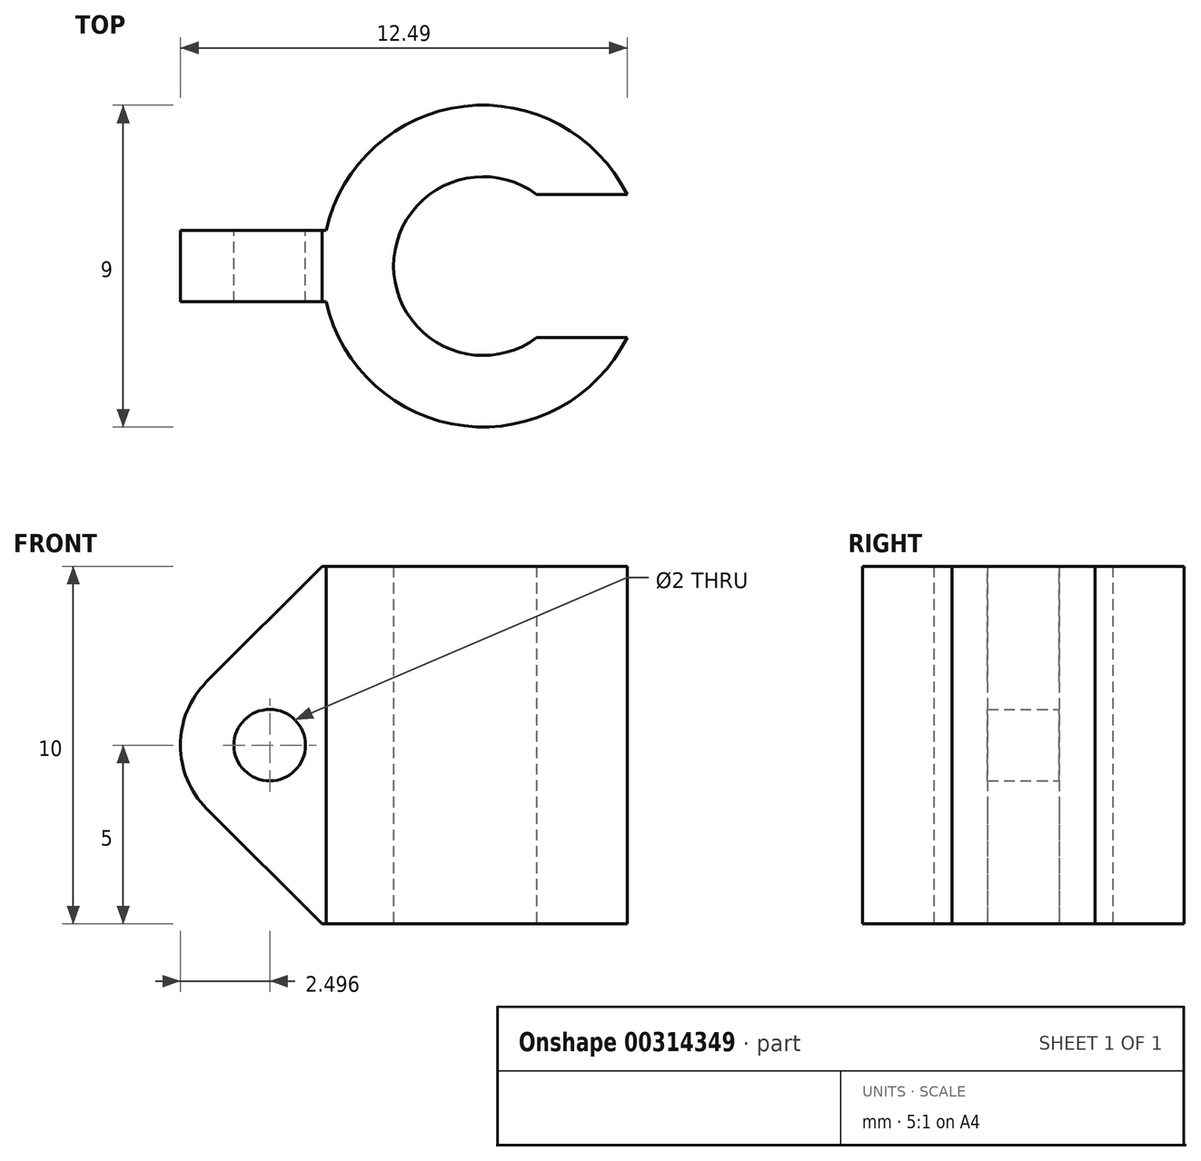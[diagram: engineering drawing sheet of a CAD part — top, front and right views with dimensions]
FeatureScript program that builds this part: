
annotation { "Feature Type Name" : "Feature", "Feature Type Description" : "" }
export const myFeature = defineFeature(function(context is Context, id is Id, definition is map)
    precondition{}
    {
        {
            var Q0;
            Q0=qCreatedBy(makeId("Top.planeOp"),FACE);
            var sketch = newSketch(context, id + "F0", { "sketchPlane" : qUnion([Q0])});
            skArc(sketch, "E0", {"start": v(4.03, 2) * mm, "mid": v(-4.5, 0) * mm, "end": v(4.03, -2) * mm});
            skArc(sketch, "E1", {"start": v(1.5, 2) * mm, "mid": v(-2.5, 0) * mm, "end": v(1.5, -2) * mm});
            skLineSegment(sketch, "E2", {"start": v(-7.9, 0) * mm, "end": v(10.8, 0) * mm, "construction": true});
            skLineSegment(sketch, "E3", {"start": v(4.03, -2) * mm, "end": v(1.5, -2) * mm});
            skLineSegment(sketch, "E4.trimOffspring", {"start": v(1.5, 2) * mm, "end": v(4.03, 2) * mm});
            skSolve(sketch);
        }
        {
            var Q0;
            Q0 = qSketchRegion(id + "F0", true);
            extrude(context, id + "F1", {"entities" : qUnion([Q0]), "depth" : 10 * mm, "offsetDistance" : 25 * mm});
        }
        {
            var Q0;
            Q0=qCreatedBy(makeId("Front.planeOp"),FACE);
            var sketch = newSketch(context, id + "F2", { "sketchPlane" : qUnion([Q0])});
            skCircle(sketch, "E5", {"center": v(-5.96, 5) * mm, "radius": 1 * mm});
            skLineSegment(sketch, "E6", {"start": v(-5.96, 5) * mm, "end": v(0, 5) * mm, "construction": true});
            skLineSegment(sketch, "E7", {"start": v(0, 0) * mm, "end": v(0, 5) * mm, "construction": true});
            skArc(sketch, "E8.0", {"start": v(-7.73, 6.77) * mm, "mid": v(-8.46, 5) * mm, "end": v(-7.73, 3.23) * mm});
            skLineSegment(sketch, "E9", {"start": v(-7.73, 6.77) * mm, "end": v(-4.5, 10) * mm});
            skLineSegment(sketch, "E10", {"start": v(-7.73, 3.23) * mm, "end": v(-4.5, 0) * mm});
            skLineSegment(sketch, "E11", {"start": v(-4.5, 0) * mm, "end": v(-4.5, 10) * mm});
            skLineSegment(sketch, "E12.bottom", {"start": v(-4.5, 10) * mm, "end": v(-3.81, 10) * mm});
            skLineSegment(sketch, "E12.top", {"start": v(-4.5, 0) * mm, "end": v(-3.81, 0) * mm});
            skLineSegment(sketch, "E12.left", {"start": v(-4.5, 10) * mm, "end": v(-4.5, 0) * mm});
            skLineSegment(sketch, "E12.right", {"start": v(-3.81, 10) * mm, "end": v(-3.81, 0) * mm});
            skSolve(sketch);
        }
        {
            var Q0;
            Q0 = qSketchRegion(id + "F2", true);
            extrude(context, id + "F3", {"entities" : qUnion([Q0]), "operationType" : NewBodyOperationType.ADD, "depth" : 2 * mm, "offsetDistance" : 25 * mm, "symmetric" : true});
        }
    });
